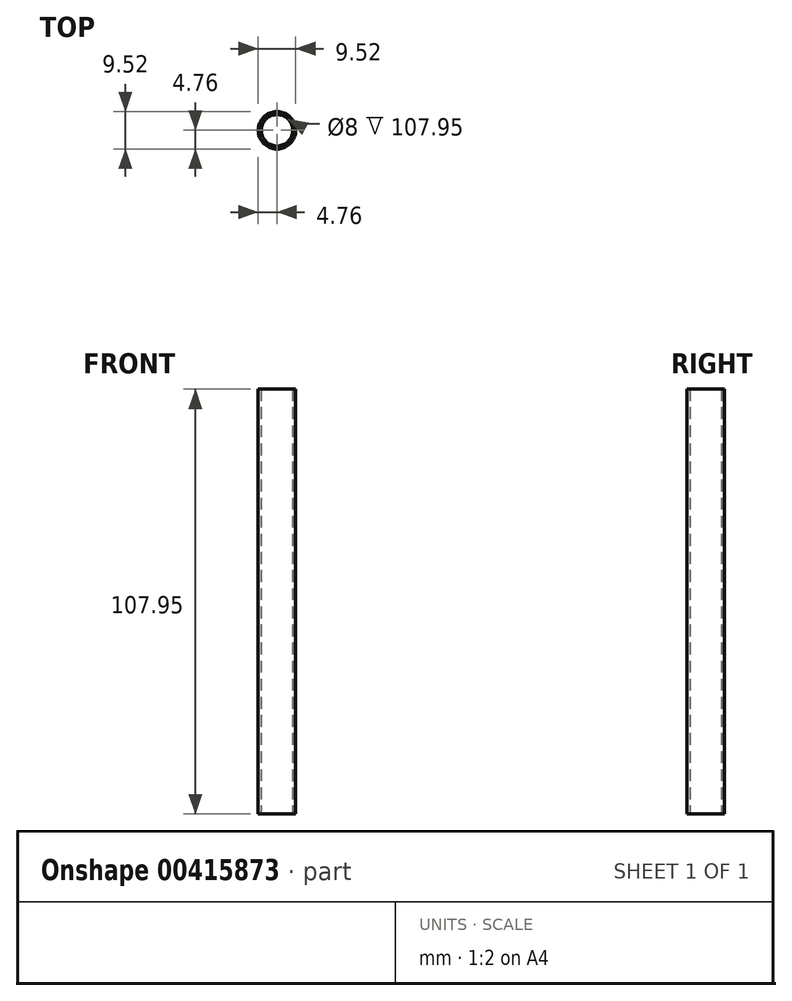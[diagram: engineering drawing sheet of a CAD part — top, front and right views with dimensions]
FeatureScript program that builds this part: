
annotation { "Feature Type Name" : "Feature", "Feature Type Description" : "" }
export const myFeature = defineFeature(function(context is Context, id is Id, definition is map)
    precondition{}
    {
        {
            var Q0;
            Q0=qCreatedBy(makeId("Top.planeOp"),FACE);
            var sketch = newSketch(context, id + "F0", { "sketchPlane" : qUnion([Q0])});
            skCircle(sketch, "E0", {"center": v(0, 0) * mm, "radius": 4.76 * mm});
            skCircle(sketch, "E1.0", {"center": v(0, 0) * mm, "radius": 4 * mm});
            skSolve(sketch);
        }
        {
            var Q0;
            Q0=qSketchRegion(id+"F0",true);
            extrude(context, id + "F1", {"entities" : qUnion([Q0]), "depth" : 107.95 * mm});
        }
    });
